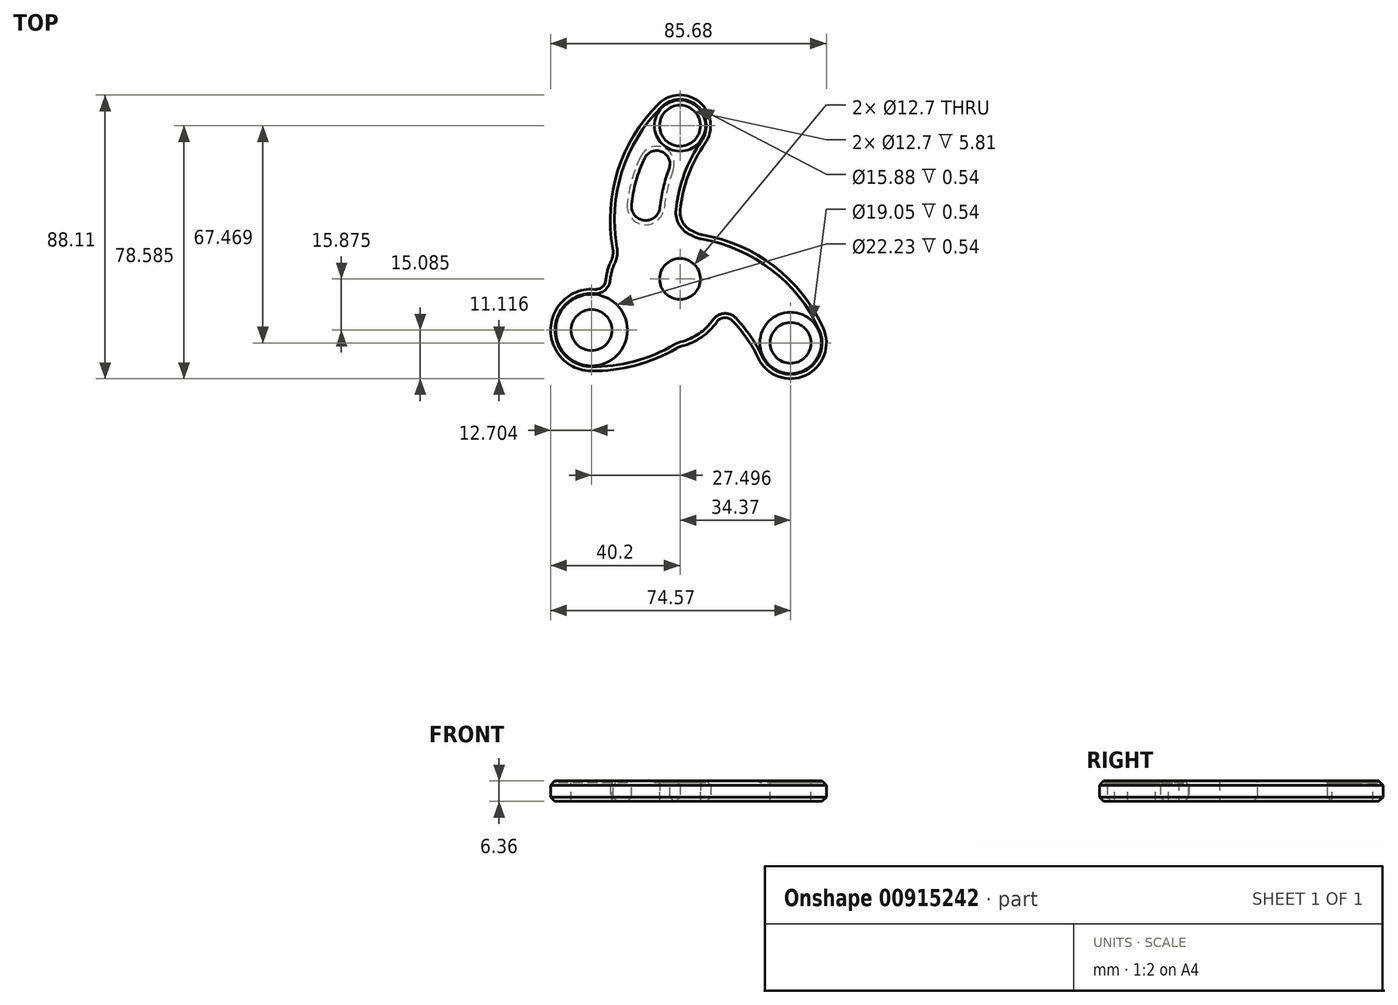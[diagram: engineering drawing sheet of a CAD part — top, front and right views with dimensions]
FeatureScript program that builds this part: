
annotation { "Feature Type Name" : "Feature", "Feature Type Description" : "" }
export const myFeature = defineFeature(function(context is Context, id is Id, definition is map)
    precondition{}
    {
        {
            var Q0;
            Q0=qCreatedBy(makeId("Top.planeOp"),FACE);
            var sketch = newSketch(context, id + "F0", { "sketchPlane" : qUnion([Q0])});
            skCircle(sketch, "E0", {"center": v(0, 0) * mm, "radius": 6.35 * mm});
            skLineSegment(sketch, "E1", {"start": v(0, 0) * mm, "end": v(0, 57.15) * mm, "construction": true});
            skCircle(sketch, "E2", {"center": v(0, 47.63) * mm, "radius": 9.53 * mm});
            skLineSegment(sketch, "E3", {"start": v(0, 0) * mm, "end": v(44, -25.4) * mm, "construction": true});
            skLineSegment(sketch, "E4", {"start": v(0, 0) * mm, "end": v(-38.5, -22.23) * mm, "construction": true});
            skCircle(sketch, "E5", {"center": v(34.37, -19.84) * mm, "radius": 11.11 * mm});
            skCircle(sketch, "E6", {"center": v(-27.5, -15.88) * mm, "radius": 12.7 * mm});
            skCircle(sketch, "E7", {"center": v(-4.12, -2.38) * mm, "radius": 19.05 * mm});
            skArc(sketch, "E8", {"start": v(-6.72, 54.37) * mm, "mid": v(-19.63, 32.65) * mm, "end": v(-20.47, 7.4) * mm});
            skArc(sketch, "E9", {"start": v(7.81, 42.18) * mm, "mid": v(1.8, 29.84) * mm, "end": v(-0.17, 16.25) * mm});
            skArc(sketch, "E10", {"start": v(44.48, -15.23) * mm, "mid": v(28.8, 4.27) * mm, "end": v(5.73, 13.92) * mm});
            skArc(sketch, "E11", {"start": v(24.34, -24.62) * mm, "mid": v(19.56, -16.8) * mm, "end": v(13.29, -10.11) * mm});
            skLineSegment(sketch, "E12", {"start": v(-6.72, 54.37) * mm, "end": v(7.81, 42.18) * mm, "construction": true});
            skLineSegment(sketch, "E13", {"start": v(24.34, -24.62) * mm, "end": v(44.48, -15.23) * mm, "construction": true});
            skArc(sketch, "E14", {"start": v(-27.69, -28.57) * mm, "mid": v(-13.46, -26.76) * mm, "end": v(-0.3, -21.04) * mm});
            skArc(sketch, "E15", {"start": v(-25.48, -3.34) * mm, "mid": v(-24.3, -3.5) * mm, "end": v(-23.13, -3.65) * mm});
            skLineSegment(sketch, "E16", {"start": v(-25.48, -3.34) * mm, "end": v(-27.69, -28.57) * mm, "construction": true});
            skSolve(sketch);
        }
        {
            var Q0;
            Q0=qCreatedBy(makeId("Top.planeOp"),FACE);
            var sketch = newSketch(context, id + "F1", { "sketchPlane" : qUnion([Q0])});
            skArc(sketch, "E17.0", {"start": v(7.81, 42.18) * mm, "mid": v(6.12, 54.92) * mm, "end": v(-6.72, 54.37) * mm});
            skArc(sketch, "E18.0", {"start": v(-6.72, 54.37) * mm, "mid": v(-19.63, 32.65) * mm, "end": v(-20.47, 7.4) * mm});
            skArc(sketch, "E19.0", {"start": v(7.81, 42.18) * mm, "mid": v(1.8, 29.84) * mm, "end": v(-0.17, 16.25) * mm});
            skArc(sketch, "E20.0", {"start": v(-20.47, 7.4) * mm, "mid": v(-22.65, 2.08) * mm, "end": v(-23.13, -3.65) * mm});
            skArc(sketch, "E21.0", {"start": v(44.48, -15.23) * mm, "mid": v(28.8, 4.27) * mm, "end": v(5.73, 13.92) * mm});
            skArc(sketch, "E22.0", {"start": v(24.34, -24.62) * mm, "mid": v(39.07, -29.92) * mm, "end": v(44.48, -15.23) * mm});
            skArc(sketch, "E23.0", {"start": v(24.34, -24.62) * mm, "mid": v(19.56, -16.8) * mm, "end": v(13.29, -10.11) * mm});
            skArc(sketch, "E24.0", {"start": v(-27.69, -28.57) * mm, "mid": v(-13.46, -26.76) * mm, "end": v(-0.3, -21.04) * mm});
            skArc(sketch, "E25.0", {"start": v(-25.48, -3.34) * mm, "mid": v(-40.15, -14.77) * mm, "end": v(-27.69, -28.57) * mm});
            skArc(sketch, "E26.0", {"start": v(-25.48, -3.34) * mm, "mid": v(-24.3, -3.5) * mm, "end": v(-23.13, -3.65) * mm});
            skCircle(sketch, "E27.0", {"center": v(0, 0) * mm, "radius": 6.35 * mm});
            skArc(sketch, "E28.trimOffspring", {"start": v(5.73, 13.92) * mm, "mid": v(2.88, 15.34) * mm, "end": v(-0.17, 16.25) * mm});
            skArc(sketch, "E29.trimOffspring", {"start": v(-0.3, -21.04) * mm, "mid": v(7.82, -17.22) * mm, "end": v(13.29, -10.11) * mm});
            skSolve(sketch);
        }
        {
            var Q0;
            Q0 = qSketchRegion(id + "F1", true);
            extrude(context, id + "F2", {"entities" : qUnion([Q0]), "endBound" : BoundingType.SYMMETRIC, "depth" : 6.35 * mm, "offsetDistance" : 25.4 * mm});
        }
        {
            var Q0;
            Q0=makeQuery(id+"F2.opExtrude","CAP_FACE",FACE,{"disambiguationData":[OSD([sQuery(id+"F1.wireOp",EDGE,"E17.0"),sQuery(id+"F1.wireOp",EDGE,"E18.0"),sQuery(id+"F1.wireOp",EDGE,"E19.0"),sQuery(id+"F1.wireOp",EDGE,"E20.0"),sQuery(id+"F1.wireOp",EDGE,"E21.0"),sQuery(id+"F1.wireOp",EDGE,"E22.0"),sQuery(id+"F1.wireOp",EDGE,"E23.0"),sQuery(id+"F1.wireOp",EDGE,"E24.0"),sQuery(id+"F1.wireOp",EDGE,"E25.0"),sQuery(id+"F1.wireOp",EDGE,"E26.0"),sQuery(id+"F1.wireOp",EDGE,"E27.0"),sQuery(id+"F1.wireOp",EDGE,"E28.trimOffspring"),sQuery(id+"F1.wireOp",EDGE,"E29.trimOffspring")])],"isStart":false});
            var sketch = newSketch(context, id + "F3", { "sketchPlane" : qUnion([Q0])});
            skCircle(sketch, "E30", {"center": v(0, 47.63) * mm, "radius": 6.35 * mm});
            skCircle(sketch, "E31", {"center": v(34.37, -19.84) * mm, "radius": 6.35 * mm});
            skCircle(sketch, "E32", {"center": v(-27.5, -15.88) * mm, "radius": 6.35 * mm});
            skSolve(sketch);
        }
        {
            var Q0;
            Q0 = qSketchRegion(id + "F3", true);
            extrude(context, id + "F4", {"entities" : qUnion([Q0]), "operationType" : NewBodyOperationType.REMOVE, "endBound" : BoundingType.THROUGH_ALL, "oppositeDirection" : true, "depth" : 25.4 * mm, "offsetDistance" : 25.4 * mm});
        }
        {
            var Q0;
            Q0=makeQuery(id+"F2.opExtrude","SWEPT_EDGE",EDGE,{"disambiguationData":[OSD([sQuery(id+"F1.wireOp",EDGE,"E18.0"),sQuery(id+"F1.wireOp",EDGE,"E20.0")])]});
            var Q1;
            Q1=makeQuery(id+"F2.opExtrude","SWEPT_EDGE",EDGE,{"disambiguationData":[OSD([sQuery(id+"F1.wireOp",EDGE,"E19.0"),sQuery(id+"F1.wireOp",EDGE,"E28.trimOffspring")])]});
            var Q2;
            Q2=makeQuery(id+"F2.opExtrude","SWEPT_EDGE",EDGE,{"disambiguationData":[OSD([sQuery(id+"F1.wireOp",EDGE,"E21.0"),sQuery(id+"F1.wireOp",EDGE,"E28.trimOffspring")])]});
            var Q3;
            Q3=makeQuery(id+"F2.opExtrude","SWEPT_EDGE",EDGE,{"disambiguationData":[OSD([sQuery(id+"F1.wireOp",EDGE,"E24.0"),sQuery(id+"F1.wireOp",EDGE,"E29.trimOffspring")])]});
            fillet(context, id + "F5", {"entities" : qUnion([Q0, Q1, Q2, Q3]), "radius" : 6.35 * mm, "tangentPropagation" : true, "allowEdgeOverflow" : false});
        }
        {
            var Q0;
            Q0=makeQuery(id+"F2.opExtrude","SWEPT_EDGE",EDGE,{"disambiguationData":[OSD([sQuery(id+"F1.wireOp",EDGE,"E23.0"),sQuery(id+"F1.wireOp",EDGE,"E29.trimOffspring")])]});
            var Q1;
            Q1=makeQuery(id+"F2.opExtrude","SWEPT_EDGE",EDGE,{"disambiguationData":[OSD([sQuery(id+"F1.wireOp",EDGE,"E20.0"),sQuery(id+"F1.wireOp",EDGE,"E26.0")])]});
            fillet(context, id + "F6", {"entities" : qUnion([Q0, Q1]), "radius" : 3.17 * mm, "tangentPropagation" : true, "allowEdgeOverflow" : false});
        }
        {
            var Q0;
            Q0=makeQuery(id+"F2.opExtrude","CAP_FACE",FACE,{"disambiguationData":[OSD([sQuery(id+"F1.wireOp",EDGE,"E17.0"),sQuery(id+"F1.wireOp",EDGE,"E18.0"),sQuery(id+"F1.wireOp",EDGE,"E19.0"),sQuery(id+"F1.wireOp",EDGE,"E20.0"),sQuery(id+"F1.wireOp",EDGE,"E21.0"),sQuery(id+"F1.wireOp",EDGE,"E22.0"),sQuery(id+"F1.wireOp",EDGE,"E23.0"),sQuery(id+"F1.wireOp",EDGE,"E24.0"),sQuery(id+"F1.wireOp",EDGE,"E25.0"),sQuery(id+"F1.wireOp",EDGE,"E26.0"),sQuery(id+"F1.wireOp",EDGE,"E27.0"),sQuery(id+"F1.wireOp",EDGE,"E28.trimOffspring"),sQuery(id+"F1.wireOp",EDGE,"E29.trimOffspring")])],"isStart":false});
            var sketch = newSketch(context, id + "F7", { "sketchPlane" : qUnion([Q0])});
            skCircle(sketch, "E33", {"center": v(-27.5, -15.88) * mm, "radius": 11.11 * mm});
            skCircle(sketch, "E34", {"center": v(34.37, -19.84) * mm, "radius": 9.53 * mm});
            skCircle(sketch, "E35", {"center": v(0, 47.63) * mm, "radius": 7.94 * mm});
            skSolve(sketch);
        }
        {
            var Q0;
            Q0 = qSketchRegion(id + "F7", true);
            extrude(context, id + "F8", {"entities" : qUnion([Q0]), "operationType" : NewBodyOperationType.REMOVE, "oppositeDirection" : true, "depth" : 0.54 * mm, "offsetDistance" : 25.4 * mm});
        }
        {
            var Q0;
            Q0=makeQuery(id+"F2.opExtrude","CAP_FACE",FACE,{"disambiguationData":[OSD([sQuery(id+"F1.wireOp",EDGE,"E17.0"),sQuery(id+"F1.wireOp",EDGE,"E18.0"),sQuery(id+"F1.wireOp",EDGE,"E19.0"),sQuery(id+"F1.wireOp",EDGE,"E20.0"),sQuery(id+"F1.wireOp",EDGE,"E21.0"),sQuery(id+"F1.wireOp",EDGE,"E22.0"),sQuery(id+"F1.wireOp",EDGE,"E23.0"),sQuery(id+"F1.wireOp",EDGE,"E24.0"),sQuery(id+"F1.wireOp",EDGE,"E25.0"),sQuery(id+"F1.wireOp",EDGE,"E26.0"),sQuery(id+"F1.wireOp",EDGE,"E27.0"),sQuery(id+"F1.wireOp",EDGE,"E28.trimOffspring"),sQuery(id+"F1.wireOp",EDGE,"E29.trimOffspring")])],"isStart":false});
            var sketch = newSketch(context, id + "F9", { "sketchPlane" : qUnion([Q0])});
            skArc(sketch, "E36.0", {"start": v(-6.72, 54.37) * mm, "mid": v(-19.32, 33.66) * mm, "end": v(-20.89, 9.47) * mm});
            skArc(sketch, "E37.0", {"start": v(7.81, 42.18) * mm, "mid": v(2.63, 32.28) * mm, "end": v(0.07, 21.4) * mm});
            skArc(sketch, "E38.0", {"start": v(7.81, 42.18) * mm, "mid": v(6.12, 54.92) * mm, "end": v(-6.72, 54.37) * mm});
            skArc(sketch, "E39.0", {"start": v(2.6, 45.8) * mm, "mid": v(-3.3, 34.54) * mm, "end": v(-6.23, 22.16) * mm});
            skArc(sketch, "E39.1", {"start": v(2.6, 45.8) * mm, "mid": v(2.04, 50.06) * mm, "end": v(-2.24, 49.87) * mm});
            skArc(sketch, "E39.2", {"start": v(-2.24, 49.87) * mm, "mid": v(-10.96, 37.6) * mm, "end": v(-15.07, 23.1) * mm});
            skLineSegment(sketch, "E40", {"start": v(-15.07, 23.1) * mm, "end": v(-6.23, 22.16) * mm, "construction": true});
            skCircle(sketch, "E41", {"center": v(-10.65, 22.63) * mm, "radius": 4.45 * mm});
            skCircle(sketch, "E42", {"center": v(-7.25, 35.77) * mm, "radius": 4.13 * mm});
            skSolve(sketch);
        }
        {
            var Q0;
            Q0=makeQuery(id+"F9.imprint","IMPRINT",FACE,{"disambiguationData":[TD([[makeQuery(id+"F9.imprint","IMPRINT",EDGE,{"derivedFrom":sQuery(id+"F9.wireOp",EDGE,"E36.0")}),1.0]])]});
            var sketch = newSketch(context, id + "F10", { "sketchPlane" : qUnion([Q0])});
            skPoint(sketch, "E43.0", {"position": v(-10.65, 22.63) * mm});
            skArc(sketch, "E44.0", {"start": v(-15.07, 23.1) * mm, "mid": v(-11.13, 18.2) * mm, "end": v(-6.23, 22.16) * mm});
            skArc(sketch, "E45.0", {"start": v(-3.38, 34.34) * mm, "mid": v(-5.65, 39.57) * mm, "end": v(-10.98, 37.55) * mm});
            skArc(sketch, "E46.0.1", {"start": v(-10.98, 37.55) * mm, "mid": v(-13.64, 30.5) * mm, "end": v(-15.07, 23.1) * mm});
            skArc(sketch, "E46.0.3", {"start": v(-6.23, 22.16) * mm, "mid": v(-5.18, 28.34) * mm, "end": v(-3.38, 34.34) * mm});
            skPoint(sketch, "E47.orphan", {"position": v(2.6, 45.8) * mm});
            skSolve(sketch);
        }
        {
            var Q0;
            Q0 = qSketchRegion(id + "F10", true);
            extrude(context, id + "F11", {"entities" : qUnion([Q0]), "operationType" : NewBodyOperationType.REMOVE, "oppositeDirection" : true, "depth" : 25.4 * mm, "offsetDistance" : 25.4 * mm});
        }
        {
            var Q0;
            Q0=makeQuery(id+"F2.opExtrude","CAP_EDGE",EDGE,{"disambiguationData":[OSD([sQuery(id+"F1.wireOp",EDGE,"E24.0")])],"isStart":false});
            var Q1;
            Q1=makeQuery(id+"F2.opExtrude","CAP_EDGE",EDGE,{"disambiguationData":[OSD([sQuery(id+"F1.wireOp",EDGE,"E24.0")])],"isStart":true});
            var Q2;
            Q2=makeQuery(id+"F11.boolean.opBoolean","COPY",EDGE,{"derivedFrom":makeQuery(id+"F11.opExtrude","CAP_EDGE",EDGE,{"disambiguationData":[OSD([sQuery(id+"F10.wireOp",EDGE,"E46.0.1")])],"isStart":true})});
            var Q3;
            Q3=makeQuery(id+"F11.boolean.opBoolean","INTERSECT",EDGE,{"derivedFrom":[makeQuery(id+"F2.opExtrude","CAP_FACE",FACE,{"disambiguationData":[OSD([sQuery(id+"F1.wireOp",EDGE,"E17.0"),sQuery(id+"F1.wireOp",EDGE,"E18.0"),sQuery(id+"F1.wireOp",EDGE,"E19.0"),sQuery(id+"F1.wireOp",EDGE,"E20.0"),sQuery(id+"F1.wireOp",EDGE,"E21.0"),sQuery(id+"F1.wireOp",EDGE,"E22.0"),sQuery(id+"F1.wireOp",EDGE,"E23.0"),sQuery(id+"F1.wireOp",EDGE,"E24.0"),sQuery(id+"F1.wireOp",EDGE,"E25.0"),sQuery(id+"F1.wireOp",EDGE,"E26.0"),sQuery(id+"F1.wireOp",EDGE,"E27.0"),sQuery(id+"F1.wireOp",EDGE,"E28.trimOffspring"),sQuery(id+"F1.wireOp",EDGE,"E29.trimOffspring")])],"isStart":true}),makeQuery(id+"F11.opExtrude","SWEPT_FACE",FACE,{"disambiguationData":[OSD([sQuery(id+"F10.wireOp",EDGE,"E45.0")])]})]});
            chamfer(context, id + "F12", {"entities" : qUnion([Q0, Q1, Q2, Q3]), "width" : 1.33 * mm, "tangentPropagation" : true});
        }
    });
